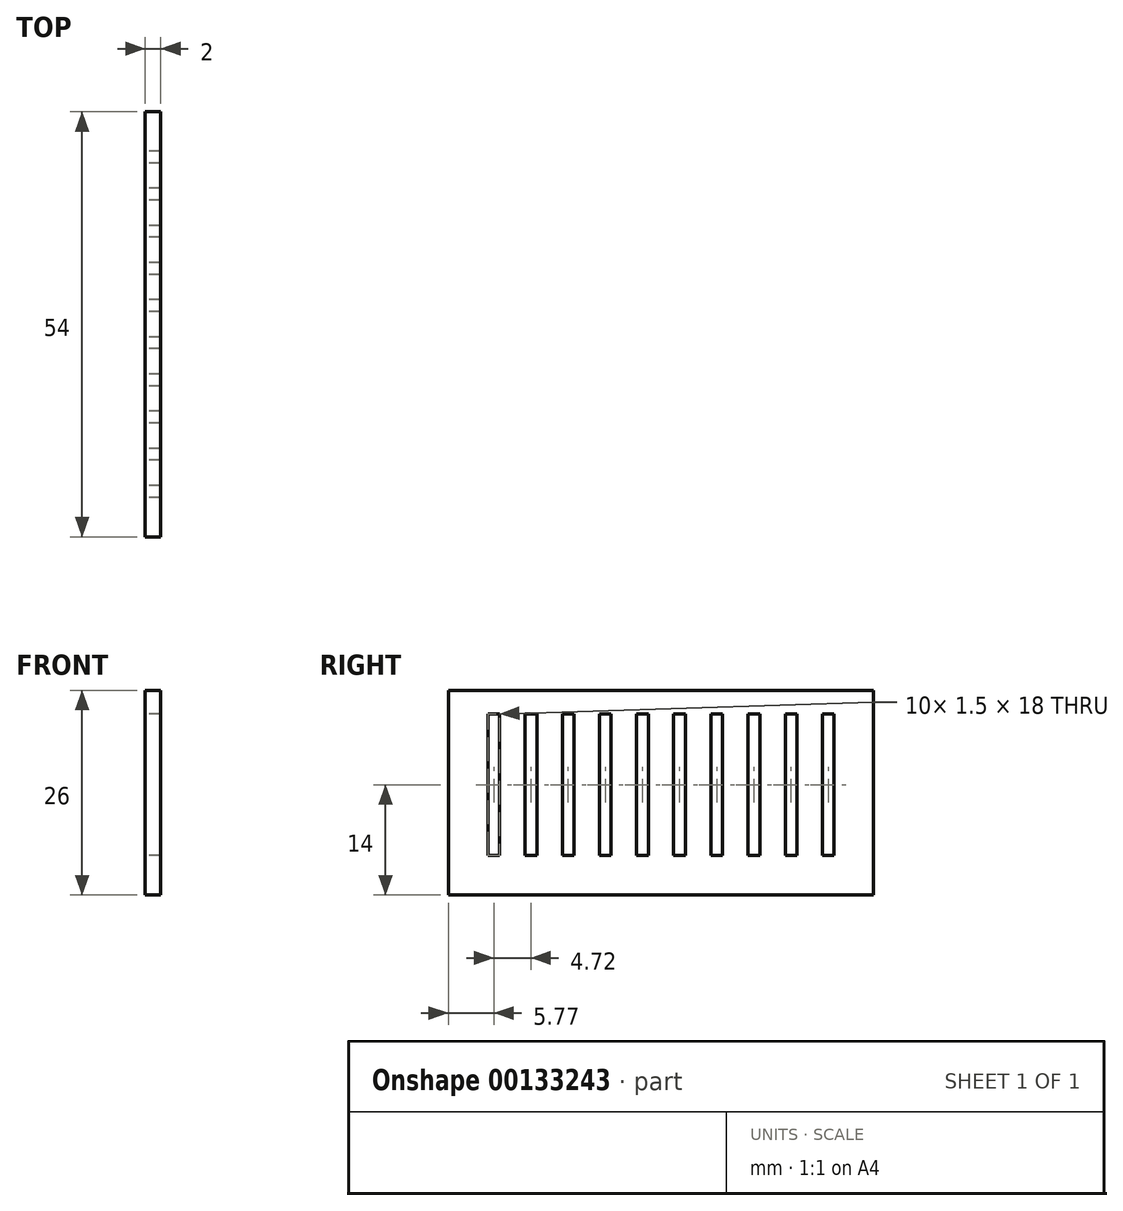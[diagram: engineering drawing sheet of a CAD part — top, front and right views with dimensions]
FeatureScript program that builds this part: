
annotation { "Feature Type Name" : "Feature", "Feature Type Description" : "" }
export const myFeature = defineFeature(function(context is Context, id is Id, definition is map)
    precondition{}
    {
        {
            var Q0;
            Q0=qCreatedBy(makeId("Right.planeOp"),FACE);
            var sketch = newSketch(context, id + "F0", { "sketchPlane" : qUnion([Q0])});
            skLineSegment(sketch, "E0.bottom", {"start": v(0, 0) * mm, "end": v(54, 0) * mm});
            skLineSegment(sketch, "E0.left", {"start": v(0, 0) * mm, "end": v(0, -26) * mm});
            skLineSegment(sketch, "E0.right", {"start": v(54, 0) * mm, "end": v(54, -26) * mm});
            skLineSegment(sketch, "E1", {"start": v(54, -26) * mm, "end": v(0, -26) * mm});
            skLineSegment(sketch, "E2.bottom", {"start": v(49, -3) * mm, "end": v(47.5, -3) * mm});
            skLineSegment(sketch, "E2.top", {"start": v(49, -21) * mm, "end": v(47.5, -21) * mm});
            skLineSegment(sketch, "E2.left", {"start": v(49, -3) * mm, "end": v(49, -21) * mm});
            skLineSegment(sketch, "E2.right", {"start": v(47.5, -3) * mm, "end": v(47.5, -21) * mm});
            skLineSegment(sketch, "E3.1.0.0", {"start": v(42.78, -3) * mm, "end": v(42.78, -21) * mm});
            skLineSegment(sketch, "E3.1.0.1", {"start": v(44.28, -3) * mm, "end": v(44.28, -21) * mm});
            skLineSegment(sketch, "E3.1.0.2", {"start": v(44.28, -3) * mm, "end": v(42.78, -3) * mm});
            skLineSegment(sketch, "E3.1.0.3", {"start": v(44.28, -21) * mm, "end": v(42.78, -21) * mm});
            skLineSegment(sketch, "E3.2.0.0", {"start": v(38.06, -3) * mm, "end": v(38.06, -21) * mm});
            skLineSegment(sketch, "E3.2.0.1", {"start": v(39.56, -3) * mm, "end": v(39.56, -21) * mm});
            skLineSegment(sketch, "E3.2.0.2", {"start": v(39.56, -3) * mm, "end": v(38.06, -3) * mm});
            skLineSegment(sketch, "E3.2.0.3", {"start": v(39.56, -21) * mm, "end": v(38.06, -21) * mm});
            skLineSegment(sketch, "E3.3.0.0", {"start": v(33.34, -3) * mm, "end": v(33.34, -21) * mm});
            skLineSegment(sketch, "E3.3.0.1", {"start": v(34.84, -3) * mm, "end": v(34.84, -21) * mm});
            skLineSegment(sketch, "E3.3.0.2", {"start": v(34.84, -3) * mm, "end": v(33.34, -3) * mm});
            skLineSegment(sketch, "E3.3.0.3", {"start": v(34.84, -21) * mm, "end": v(33.34, -21) * mm});
            skLineSegment(sketch, "E3.4.0.0", {"start": v(28.62, -3) * mm, "end": v(28.62, -21) * mm});
            skLineSegment(sketch, "E3.4.0.1", {"start": v(30.12, -3) * mm, "end": v(30.12, -21) * mm});
            skLineSegment(sketch, "E3.4.0.2", {"start": v(30.12, -3) * mm, "end": v(28.62, -3) * mm});
            skLineSegment(sketch, "E3.4.0.3", {"start": v(30.12, -21) * mm, "end": v(28.62, -21) * mm});
            skLineSegment(sketch, "E3.5.0.0", {"start": v(23.9, -3) * mm, "end": v(23.9, -21) * mm});
            skLineSegment(sketch, "E3.5.0.1", {"start": v(25.4, -3) * mm, "end": v(25.4, -21) * mm});
            skLineSegment(sketch, "E3.5.0.2", {"start": v(25.4, -3) * mm, "end": v(23.9, -3) * mm});
            skLineSegment(sketch, "E3.5.0.3", {"start": v(25.4, -21) * mm, "end": v(23.9, -21) * mm});
            skLineSegment(sketch, "E3.6.0.0", {"start": v(19.18, -3) * mm, "end": v(19.18, -21) * mm});
            skLineSegment(sketch, "E3.6.0.1", {"start": v(20.68, -3) * mm, "end": v(20.68, -21) * mm});
            skLineSegment(sketch, "E3.6.0.2", {"start": v(20.68, -3) * mm, "end": v(19.18, -3) * mm});
            skLineSegment(sketch, "E3.6.0.3", {"start": v(20.68, -21) * mm, "end": v(19.18, -21) * mm});
            skLineSegment(sketch, "E3.7.0.0", {"start": v(14.46, -3) * mm, "end": v(14.46, -21) * mm});
            skLineSegment(sketch, "E3.7.0.1", {"start": v(15.96, -3) * mm, "end": v(15.96, -21) * mm});
            skLineSegment(sketch, "E3.7.0.2", {"start": v(15.96, -3) * mm, "end": v(14.46, -3) * mm});
            skLineSegment(sketch, "E3.7.0.3", {"start": v(15.96, -21) * mm, "end": v(14.46, -21) * mm});
            skLineSegment(sketch, "E3.8.0.0", {"start": v(9.74, -3) * mm, "end": v(9.74, -21) * mm});
            skLineSegment(sketch, "E3.8.0.1", {"start": v(11.24, -3) * mm, "end": v(11.24, -21) * mm});
            skLineSegment(sketch, "E3.8.0.2", {"start": v(11.24, -3) * mm, "end": v(9.74, -3) * mm});
            skLineSegment(sketch, "E3.8.0.3", {"start": v(11.24, -21) * mm, "end": v(9.74, -21) * mm});
            skLineSegment(sketch, "E3.9.0.0", {"start": v(5.02, -3) * mm, "end": v(5.02, -21) * mm});
            skLineSegment(sketch, "E3.9.0.1", {"start": v(6.52, -3) * mm, "end": v(6.52, -21) * mm});
            skLineSegment(sketch, "E3.9.0.2", {"start": v(6.52, -3) * mm, "end": v(5.02, -3) * mm});
            skLineSegment(sketch, "E3.9.0.3", {"start": v(6.52, -21) * mm, "end": v(5.02, -21) * mm});
            skLineSegment(sketch, "E3.direction1", {"start": v(47.5, -21) * mm, "end": v(42.78, -21) * mm, "construction": true});
            skSolve(sketch);
        }
        {
            var Q0;
            Q0=makeQuery(id+"F0.imprint","IMPRINT",FACE,{"disambiguationData":[TD([[makeQuery(id+"F0.imprint","IMPRINT",EDGE,{"derivedFrom":sQuery(id+"F0.wireOp",EDGE,"E0.bottom")}),-1.0]])]});
            extrude(context, id + "F1", {"entities" : qUnion([Q0]), "depth" : 2 * mm});
        }
    });
